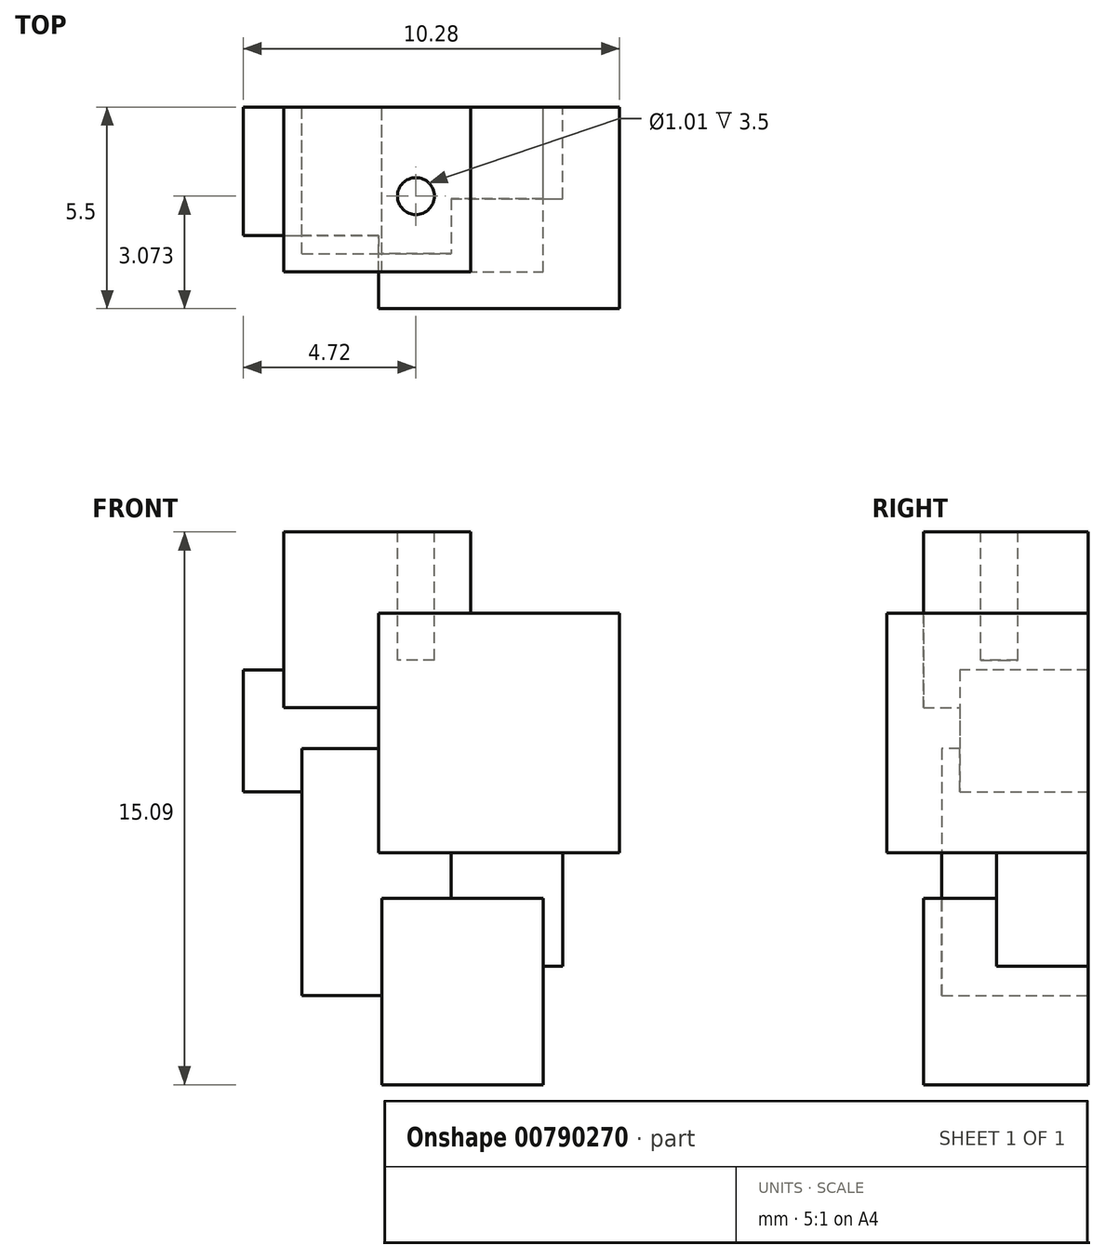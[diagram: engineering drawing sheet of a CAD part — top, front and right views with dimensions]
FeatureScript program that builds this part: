
annotation { "Feature Type Name" : "Feature", "Feature Type Description" : "" }
export const myFeature = defineFeature(function(context is Context, id is Id, definition is map)
    precondition{}
    {
        {
            var Q0;
            Q0=qCreatedBy(makeId("Front.planeOp"),FACE);
            var sketch = newSketch(context, id + "F0", { "sketchPlane" : qUnion([Q0])});
            skLineSegment(sketch, "E0.bottom", {"start": v(-52.71, 33.5) * mm, "end": v(-47.6, 33.5) * mm});
            skLineSegment(sketch, "E0.top", {"start": v(-52.71, 28.7) * mm, "end": v(-47.6, 28.7) * mm});
            skLineSegment(sketch, "E0.left", {"start": v(-52.71, 33.5) * mm, "end": v(-52.71, 28.7) * mm});
            skLineSegment(sketch, "E0.right", {"start": v(-47.6, 33.5) * mm, "end": v(-47.6, 28.7) * mm});
            skSolve(sketch);
        }
        {
            var Q0;
            Q0=makeQuery(id+"F0.imprint","IMPRINT",FACE,{"disambiguationData":[TD([[makeQuery(id+"F0.imprint","IMPRINT",EDGE,{"derivedFrom":sQuery(id+"F0.wireOp",EDGE,"E0.bottom")}),-1.0]])]});
            extrude(context, id + "F1", {"entities" : qUnion([Q0]), "depth" : 4.5 * mm, "offsetDistance" : 25 * mm});
        }
        {
            var Q0;
            Q0=qCreatedBy(makeId("Front.planeOp"),FACE);
            var sketch = newSketch(context, id + "F2", { "sketchPlane" : qUnion([Q0])});
            skLineSegment(sketch, "E1.bottom", {"start": v(-50.12, 31.28) * mm, "end": v(-43.54, 31.28) * mm});
            skLineSegment(sketch, "E1.top", {"start": v(-50.12, 24.75) * mm, "end": v(-43.54, 24.75) * mm});
            skLineSegment(sketch, "E1.left", {"start": v(-50.12, 31.28) * mm, "end": v(-50.12, 24.75) * mm});
            skLineSegment(sketch, "E1.right", {"start": v(-43.54, 31.28) * mm, "end": v(-43.54, 24.75) * mm});
            skSolve(sketch);
        }
        {
            var Q0;
            Q0=qCreatedBy(makeId("Front.planeOp"),FACE);
            var sketch = newSketch(context, id + "F3", { "sketchPlane" : qUnion([Q0])});
            skLineSegment(sketch, "E2.bottom", {"start": v(-53.82, 29.73) * mm, "end": v(-49.16, 29.73) * mm});
            skLineSegment(sketch, "E2.top", {"start": v(-53.82, 26.4) * mm, "end": v(-49.16, 26.4) * mm});
            skLineSegment(sketch, "E2.left", {"start": v(-53.82, 29.73) * mm, "end": v(-53.82, 26.4) * mm});
            skLineSegment(sketch, "E2.right", {"start": v(-49.16, 29.73) * mm, "end": v(-49.16, 26.4) * mm});
            skSolve(sketch);
        }
        {
            var Q0;
            Q0=qCreatedBy(makeId("Front.planeOp"),FACE);
            var sketch = newSketch(context, id + "F4", { "sketchPlane" : qUnion([Q0])});
            skLineSegment(sketch, "E3.bottom", {"start": v(-52.21, 27.59) * mm, "end": v(-48.14, 27.59) * mm});
            skLineSegment(sketch, "E3.top", {"start": v(-52.21, 20.84) * mm, "end": v(-48.14, 20.84) * mm});
            skLineSegment(sketch, "E3.left", {"start": v(-52.21, 27.59) * mm, "end": v(-52.21, 20.84) * mm});
            skLineSegment(sketch, "E3.right", {"start": v(-48.14, 27.59) * mm, "end": v(-48.14, 20.84) * mm});
            skSolve(sketch);
        }
        {
            var Q0;
            Q0=qCreatedBy(makeId("Front.planeOp"),FACE);
            var sketch = newSketch(context, id + "F5", { "sketchPlane" : qUnion([Q0])});
            skLineSegment(sketch, "E4.bottom", {"start": v(-49.37, 25.77) * mm, "end": v(-45.1, 25.77) * mm});
            skLineSegment(sketch, "E4.top", {"start": v(-49.37, 21.64) * mm, "end": v(-45.1, 21.64) * mm});
            skLineSegment(sketch, "E4.left", {"start": v(-49.37, 25.77) * mm, "end": v(-49.37, 21.64) * mm});
            skLineSegment(sketch, "E4.right", {"start": v(-45.1, 25.77) * mm, "end": v(-45.1, 21.64) * mm});
            skSolve(sketch);
        }
        {
            var Q0;
            Q0=makeQuery(id+"F2.imprint","IMPRINT",FACE,{"disambiguationData":[TD([[makeQuery(id+"F2.imprint","IMPRINT",EDGE,{"derivedFrom":sQuery(id+"F2.wireOp",EDGE,"E1.bottom")}),-1.0]])]});
            extrude(context, id + "F6", {"entities" : qUnion([Q0]), "operationType" : NewBodyOperationType.ADD, "depth" : 5.5 * mm, "offsetDistance" : 25 * mm});
        }
        {
            var Q0;
            Q0=makeQuery(id+"F3.imprint","IMPRINT",FACE,{"disambiguationData":[TD([[makeQuery(id+"F3.imprint","IMPRINT",EDGE,{"derivedFrom":sQuery(id+"F3.wireOp",EDGE,"E2.bottom")}),-1.0]])]});
            extrude(context, id + "F7", {"entities" : qUnion([Q0]), "operationType" : NewBodyOperationType.ADD, "depth" : 3.5 * mm, "offsetDistance" : 25 * mm});
        }
        {
            var Q0;
            Q0=qCreatedBy(makeId("Front.planeOp"),FACE);
            var sketch = newSketch(context, id + "F8", { "sketchPlane" : qUnion([Q0])});
            skLineSegment(sketch, "E5.bottom", {"start": v(-50.03, 23.5) * mm, "end": v(-45.63, 23.5) * mm});
            skLineSegment(sketch, "E5.top", {"start": v(-50.03, 18.4) * mm, "end": v(-45.63, 18.4) * mm});
            skLineSegment(sketch, "E5.left", {"start": v(-50.03, 23.5) * mm, "end": v(-50.03, 18.4) * mm});
            skLineSegment(sketch, "E5.right", {"start": v(-45.63, 23.5) * mm, "end": v(-45.63, 18.4) * mm});
            skSolve(sketch);
        }
        {
            var Q0;
            Q0=makeQuery(id+"F4.imprint","IMPRINT",FACE,{"disambiguationData":[TD([[makeQuery(id+"F4.imprint","IMPRINT",EDGE,{"derivedFrom":sQuery(id+"F4.wireOp",EDGE,"E3.bottom")}),-1.0]])]});
            extrude(context, id + "F9", {"entities" : qUnion([Q0]), "operationType" : NewBodyOperationType.ADD, "depth" : 4 * mm, "offsetDistance" : 25 * mm});
        }
        {
            var Q0;
            Q0=makeQuery(id+"F5.imprint","IMPRINT",FACE,{"disambiguationData":[TD([[makeQuery(id+"F5.imprint","IMPRINT",EDGE,{"derivedFrom":sQuery(id+"F5.wireOp",EDGE,"E4.bottom")}),-1.0]])]});
            extrude(context, id + "F10", {"entities" : qUnion([Q0]), "operationType" : NewBodyOperationType.ADD, "depth" : 2.5 * mm, "offsetDistance" : 25 * mm});
        }
        {
            var Q0;
            Q0=makeQuery(id+"F8.imprint","IMPRINT",FACE,{"disambiguationData":[TD([[makeQuery(id+"F8.imprint","IMPRINT",EDGE,{"derivedFrom":sQuery(id+"F8.wireOp",EDGE,"E5.bottom")}),-1.0]])]});
            extrude(context, id + "F11", {"entities" : qUnion([Q0]), "operationType" : NewBodyOperationType.ADD, "depth" : 4.5 * mm, "offsetDistance" : 25 * mm});
        }
        {
            var Q0;
            Q0=makeQuery(id+"F1.opExtrude","SWEPT_FACE",FACE,{"disambiguationData":[OSD([sQuery(id+"F0.wireOp",EDGE,"E0.bottom")])]});
            var sketch = newSketch(context, id + "F12", { "sketchPlane" : qUnion([Q0])});
            skCircle(sketch, "E6", {"center": v(-49.1, -2.43) * mm, "radius": 0.5 * mm});
            skSolve(sketch);
        }
        {
            var Q0;
            Q0=makeQuery(id+"F12.imprint","IMPRINT",FACE,{"disambiguationData":[TD([[makeQuery(id+"F12.imprint","IMPRINT",EDGE,{"derivedFrom":sQuery(id+"F12.wireOp",EDGE,"E6")}),1.0]])]});
            extrude(context, id + "F13", {"entities" : qUnion([Q0]), "operationType" : NewBodyOperationType.REMOVE, "oppositeDirection" : true, "depth" : 3.5 * mm, "offsetDistance" : 25 * mm});
        }
    });
